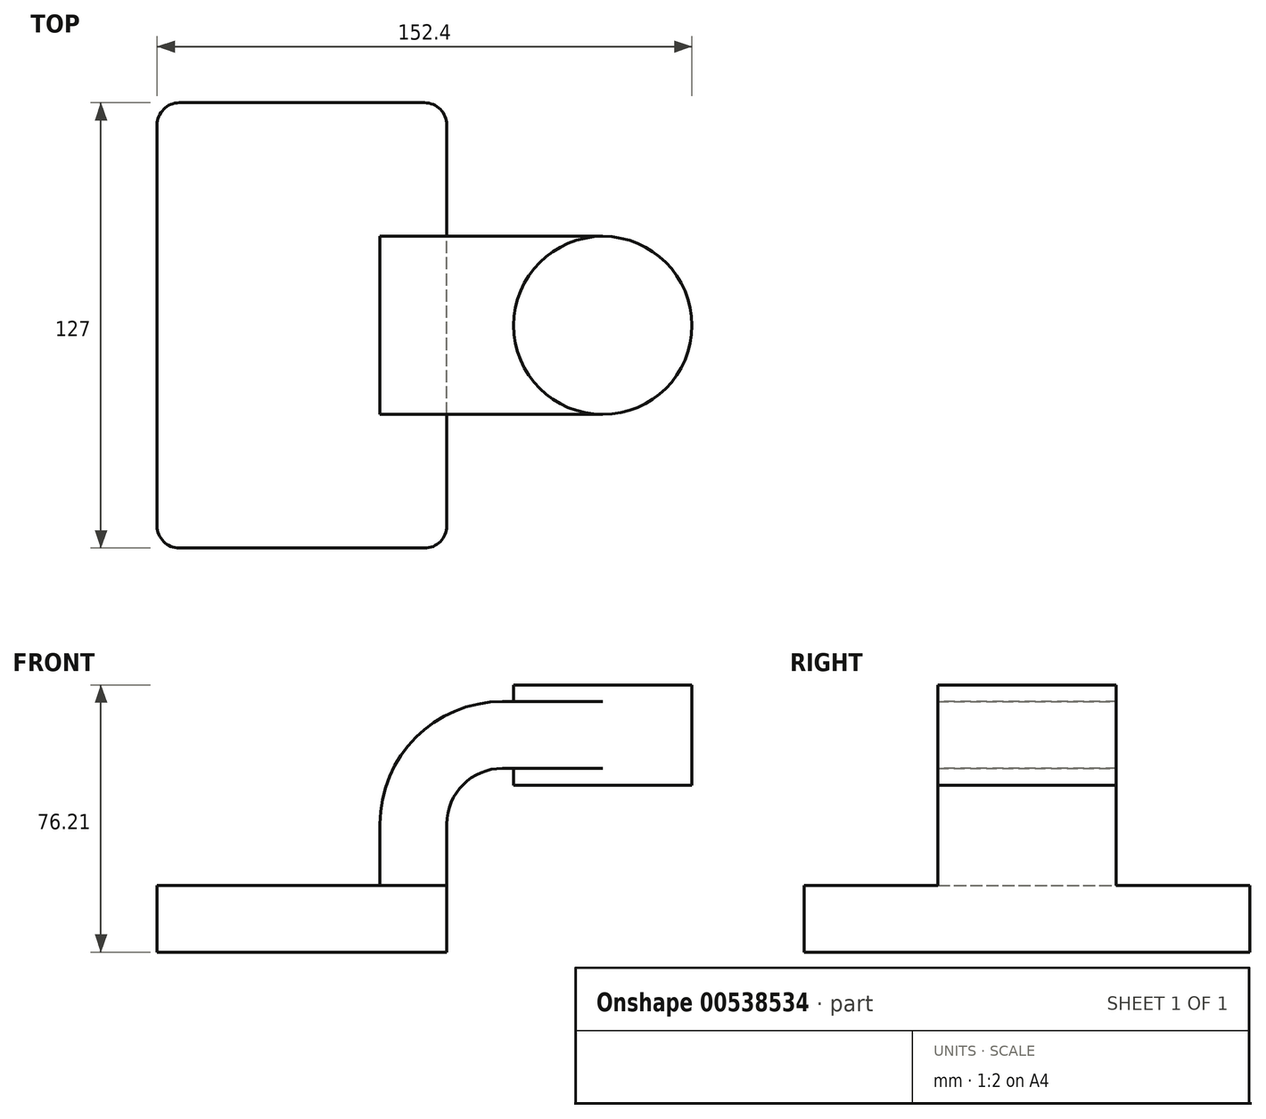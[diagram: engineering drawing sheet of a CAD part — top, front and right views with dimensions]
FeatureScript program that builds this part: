
annotation { "Feature Type Name" : "Feature", "Feature Type Description" : "" }
export const myFeature = defineFeature(function(context is Context, id is Id, definition is map)
    precondition{}
    {
        {
            var Q0;
            Q0=qCreatedBy(makeId("Front.planeOp"),FACE);
            var sketch = newSketch(context, id + "F0", { "sketchPlane" : qUnion([Q0])});
            skLineSegment(sketch, "E0.bottom", {"start": v(41.27, 9.53) * mm, "end": v(-41.28, 9.53) * mm});
            skLineSegment(sketch, "E0.top", {"start": v(41.28, -9.53) * mm, "end": v(-41.28, -9.53) * mm});
            skLineSegment(sketch, "E0.left", {"start": v(41.27, 9.53) * mm, "end": v(41.27, -9.52) * mm});
            skLineSegment(sketch, "E0.right", {"start": v(-41.28, 9.52) * mm, "end": v(-41.28, -9.53) * mm});
            skPoint(sketch, "E0.middle", {"position": v(0, 0) * mm});
            skLineSegment(sketch, "E1.bottom", {"start": v(111.12, 66.67) * mm, "end": v(60.32, 66.67) * mm});
            skLineSegment(sketch, "E1.top", {"start": v(111.12, 38.1) * mm, "end": v(60.32, 38.1) * mm});
            skLineSegment(sketch, "E1.left", {"start": v(111.12, 66.68) * mm, "end": v(111.12, 38.1) * mm});
            skLineSegment(sketch, "E1.right", {"start": v(60.32, 66.68) * mm, "end": v(60.32, 38.1) * mm});
            skPoint(sketch, "E1.middle", {"position": v(85.72, 52.39) * mm});
            skLineSegment(sketch, "E2", {"start": v(41.27, 9.53) * mm, "end": v(41.27, 27) * mm});
            skArc(sketch, "E3", {"start": v(41.27, 27) * mm, "mid": v(45.92, 38.23) * mm, "end": v(57.15, 42.88) * mm});
            skLineSegment(sketch, "E4", {"start": v(57.15, 42.88) * mm, "end": v(85.72, 42.88) * mm});
            skLineSegment(sketch, "E5.0", {"start": v(57.15, 61.93) * mm, "end": v(85.72, 61.93) * mm});
            skArc(sketch, "E5.1", {"start": v(22.22, 27) * mm, "mid": v(32.45, 51.7) * mm, "end": v(57.15, 61.93) * mm});
            skLineSegment(sketch, "E5.2", {"start": v(22.22, 9.52) * mm, "end": v(22.22, 27) * mm});
            skLineSegment(sketch, "E6", {"start": v(85.72, 66.67) * mm, "end": v(85.72, 38.1) * mm});
            skFitSpline(sketch, "E7", {"points": [v(-41.28, 9.53) * mm, v(57.15, 61.93) * mm], "startDerivative": vector(0, 41.4) * mm, "endDerivative": vector(136.1, 0) * mm});
            skSolve(sketch);
        }
        {
            var Q0;
            {var subQ1=sQuery(id+"F0.wireOp",EDGE,"E2");Q0=makeQuery(id+"F0.imprint","IMPRINT",FACE,{"disambiguationData":[TD([[makeQuery(id+"F0.imprint","IMPRINT",EDGE,{"derivedFrom":subQ1}),1.0]])]});}
            var Q1;
            {var subQ0=sQuery(id+"F0.wireOp",EDGE,"E5.0");var subQ1=sQuery(id+"F0.wireOp",EDGE,"E1.right");var subQ2=makeQuery(id+"F0.imprint","INTERSECT",VERTEX,{"derivedFrom":[subQ1,subQ0]});Q1=makeQuery(id+"F0.imprint","IMPRINT",FACE,{"disambiguationData":[TD([[makeQuery(id+"F0.imprint","IMPRINT",EDGE,{"disambiguationData":[TD([[subQ2,-1.0]])],"derivedFrom":subQ1}),1.0]])]});}
            extrude(context, id + "F1", {"entities" : qUnion([Q0, Q1]), "endBound" : BoundingType.SYMMETRIC, "depth" : 50.8 * mm, "offsetDistance" : 25.4 * mm});
        }
        {
            var Q0;
            Q0=makeQuery(id+"F0.imprint","IMPRINT",FACE,{"disambiguationData":[TD([[makeQuery(id+"F0.imprint","IMPRINT",EDGE,{"derivedFrom":sQuery(id+"F0.wireOp",EDGE,"E0.top")}),-1.0]])]});
            extrude(context, id + "F2", {"entities" : qUnion([Q0]), "operationType" : NewBodyOperationType.ADD, "endBound" : BoundingType.SYMMETRIC, "depth" : 127 * mm, "offsetDistance" : 25.4 * mm});
        }
        {
            var Q0;
            Q0=makeQuery(id+"F0.imprint","IMPRINT",FACE,{"disambiguationData":[TD([[makeQuery(id+"F0.imprint","IMPRINT",EDGE,{"derivedFrom":sQuery(id+"F0.wireOp",EDGE,"E5.1")}),1.0]])]});
            extrude(context, id + "F3", {"entities" : qUnion([Q0]), "operationType" : NewBodyOperationType.ADD, "endBound" : BoundingType.SYMMETRIC, "depth" : 25.4 * mm, "offsetDistance" : 25.4 * mm});
        }
        {
            var Q0;
            {var subQ4=sQuery(id+"F0.wireOp",EDGE,"E1.left");Q0=makeQuery(id+"F0.imprint","IMPRINT",FACE,{"disambiguationData":[TD([[makeQuery(id+"F0.imprint","IMPRINT",EDGE,{"derivedFrom":subQ4}),-1.0]])]});}
            var Q1;
            Q1=sQuery(id+"F0.wireOp",EDGE,"E1.left");
            var Q2;
            Q2=sQuery(id+"F0.wireOp",EDGE,"E1.bottom");
            var Q3;
            Q3=sQuery(id+"F0.wireOp",EDGE,"E1.right");
            var Q4;
            Q4=sQuery(id+"F0.wireOp",EDGE,"E1.top");
            var Q5;
            Q5=sQuery(id+"F0.wireOp",EDGE,"E6");
            revolve(context, id + "F4", {"operationType" : NewBodyOperationType.ADD, "entities" : qUnion([Q0]), "surfaceEntities" : qUnion([Q1, Q2, Q3, Q4]), "axis" : qUnion([Q5]), "revolveType" : RevolveType.FULL});
        }
        {
            var Q0;
            Q0=makeQuery(id+"F2.opExtrude","CAP_EDGE",EDGE,{"disambiguationData":[OSD([sQuery(id+"F0.wireOp",EDGE,"E0.left")])],"isStart":false});
            var Q1;
            Q1=makeQuery(id+"F2.opExtrude","CAP_EDGE",EDGE,{"disambiguationData":[OSD([sQuery(id+"F0.wireOp",EDGE,"E0.right")])],"isStart":false});
            var Q2;
            Q2=makeQuery(id+"F2.opExtrude","CAP_EDGE",EDGE,{"disambiguationData":[OSD([sQuery(id+"F0.wireOp",EDGE,"E0.right")])],"isStart":true});
            var Q3;
            Q3=makeQuery(id+"F2.opExtrude","CAP_EDGE",EDGE,{"disambiguationData":[OSD([sQuery(id+"F0.wireOp",EDGE,"E0.left")])],"isStart":true});
            fillet(context, id + "F5", {"entities" : qUnion([Q0, Q1, Q2, Q3]), "radius" : 6.35 * mm, "tangentPropagation" : true, "allowEdgeOverflow" : false});
        }
    });
